# Revit family: Indoor_Table Lamp_Santa&Cole_Trípode
name_source: partatom
category: Luminarias
revit_build: Autodesk Revit 2018 (Build: 20190510_1515(x64)
units: mm (PartAtom-declared; Revit-internal decimal feet)

## family parameters
Compartido = No
Corte con vacíos al cargar = No
Cota de conector redondo = Diámetro de uso
Número OmniClass = 23.80.70.00
Origen de luz = Sí
Punto de cálculo de habitación = No
Se basa en plano de trabajo = No
Siempre vertical = Sí
Tipo de pieza = Normal
Título OmniClass = Lighting

## types (12) — shared parameters
Assembly instructions - CE = https://www.santacole.com
Assembly instructions - UL = https://www.santacole.com
Cambio de temperatura de color de luz atenuada = <Ninguno>
Energy Label = https://www.santacole.com
Fabricante = Santa & Cole
Filtro de color = 16777215
Manufacturer website = http://www.santacole.com
Modelo = Trípode
Tamaño de símbolo de origen de luz = 50 mm  [stored 0.164042 ft]
Technical Information = https://www.santacole.com
URL = https://www.santacole.com

## per-type parameters (varying)
| type | Carga aparente | Code | Lampshade Material | Light source elevation | Load | Visibility_Trípode G6 | Visibility_Trípode M3 |
| Trípode G6 - Natural Ribbon | 10 VA | TG611+TG6Mx | Santa & Cole - Natural Ribbon | 665 mm | 10 W | Sí | No |
| Trípode G6 - Red-amber Ribbon | 10 VA | TG611+TG6Mx | Santa & Cole - Red-amber Ribbon | 665 mm | 10 W | Sí | No |
| Trípode G6 - Black Ribbon | 10 VA | TG611+TG6Mx | Santa & Cole - Black Ribbon | 665 mm | 10 W | Sí | No |
| Trípode G6 - Terracota Raw Color Ribbon | 10 VA | TG611+TG6Mx | Santa & Cole - Terracota Raw Color Ribbon | 665 mm | 10 W | Sí | No |
| Trípode G6 - Mustard Raw Color Ribbon | 10 VA | TG611+TG6Mx | Santa & Cole - Mustard Raw Color Ribbon | 665 mm | 10 W | Sí | No |
| Trípode G6 - Green Raw Color Ribbon | 10 VA | TG611+TG6Mx | Santa & Cole - Green Raw Color Ribbon | 665 mm | 10 W | Sí | No |
| Trípode M3 - Black Ribbon | 6 VA | TM311+TM3Mx | Santa & Cole - Black Ribbon | 445 mm | 6 W | No | Sí |
| Trípode M3 - Natural Ribbon | 6 VA | TM311+TM3Mx | Santa & Cole - Natural Ribbon | 445 mm | 6 W | No | Sí |
| Trípode M3 - Red-amber Ribbon | 6 VA | TM311+TM3Mx | Santa & Cole - Red-amber Ribbon | 445 mm | 6 W | No | Sí |
| Trípode M3 - Terracota Raw Color Ribbon | 6 VA | TM311+TM3Mx | Santa & Cole - Terracota Raw Color Ribbon | 445 mm | 6 W | No | Sí |
| Trípode M3 - Mustard Raw Color Ribbon | 6 VA | TM311+TM3Mx | Santa & Cole - Mustard Raw Color Ribbon | 445 mm | 6 W | No | Sí |
| Trípode M3 - Green Raw Color Ribbon | 6 VA | TM311+TM3Mx | Santa & Cole - Green Raw Color Ribbon | 445 mm | 6 W | No | Sí |

note: [stored X ft] marks values corroborated as IEEE doubles in the binary element streams (Revit-internal decimal feet)

## geometry (parser evidence)
native form markers: Sweep x1
no freeform markers — native parametric forms only
